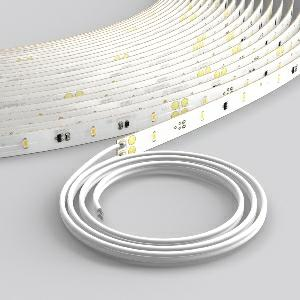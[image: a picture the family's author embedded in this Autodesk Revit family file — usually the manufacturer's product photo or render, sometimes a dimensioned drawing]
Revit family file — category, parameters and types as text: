
# Revit family: less_is_more_flex_982742_000_8f4c
name_source: partatom
category: Lighting Fixtures
units: mm (PartAtom-declared; Revit-internal decimal feet)

## family parameters
Cut with Voids When Loaded = No
Host = Face
Light Source = No
Part Type = Normal
Room Calculation Point = No
Round Connector Dimension = Use Diameter
Shared = No

## types (1)
- LESS IS MORE FLEX (1 x LED Modul 830, 1940 lm, 3000)
    Apparent Load = 16 VA
    CIE Flux Codes = 45 77 96 100 100
    Color Rendering = 80
    Color Temperature = 3000
    Default Elevation = 1800 mm
    Description = Series: LESS IS MORE FLEX
Flexible, energy-saving LED strip on a reel for maximum variety with a modular system. Luminous flux per meter 1940 lm. Lamps rating per meter 15.5 W. 140 LEDs per meter (LED Pitch 7.1 mm). LED strip length 5 m on reel. Can be cut every 100 mm. Mounting using thermal double-sided tape. Very easy installation thanks to Plug+Play connection. Pre-wired with 500 mm connection cable. Modular design: please order aluminium profile, plastic diffusers, end caps, mounting accessories, infeeds, junctions and ballasts separately. 
Length: 5000 mm
Width: 8 mm
Height: 1.5 mm
Lamp: LED
Socket: without socket
Colour temperature: 3000K
Colour rendering index (CRI): 80
System power: 78 W
Rated luminous flux: 9700 lm
Beam angle Down: 122°
Luminous efficiency: 124 lm/W
Protection class: III
Type of protection: IP 00
    Height = 2 mm  [stored 0.00656168 ft]
    Lamp = 1 x LED Modul 830
    Lamp Light Flux = 1940 lm
    Lamp count = 1
    Length = 5000 mm
    Lifetime = 50000 h
    Luminous efficacy = 124 lm/W
    Manufacturer = RZB
    ModVariant = No
    Model = 982742.000
    Mounting Place = Ceiling, Wall
    Mounting Type = Surface mounted
    Number of Poles = 1
    OnlyDefault = Yes
    Power Factor = 1
    Product Name = LESS IS MORE FLEX
    Product group = Surface mounted LED linear luminaires
    ProductGroupID = 307
    Protection Class = Safety extra-low voltage
    Protection Degree = IP 20
    RLX_Detail_Level = 1
    RLX_Emergency_Light_Flux = 0 lm
    RLX_Emergency_Type = 0
    RLX_Emergency_Type_DB = No
    RlxData = <blob elided: 91857 chars, md5=12bc229d>
    Socket = socket
    Standby Power = 0 W
    System Light Flux = 1940 lm
    System Power = 16 W
    Type Comments = ALEA SPOT
    Type Image = 982540.000.jpg
    URL = http://relux.com
    VarID = ---
    Voltage = 24 V
    Voltage Range = 24 V
    Weight = 0.00 kg
    Width = 8 mm  [stored 0.0262467 ft]

note: [stored X ft] marks values corroborated as IEEE doubles in the binary element streams (Revit-internal decimal feet)

## geometry (parser evidence)
native form markers: Blend x4, Sweep x11
no freeform markers — native parametric forms only
